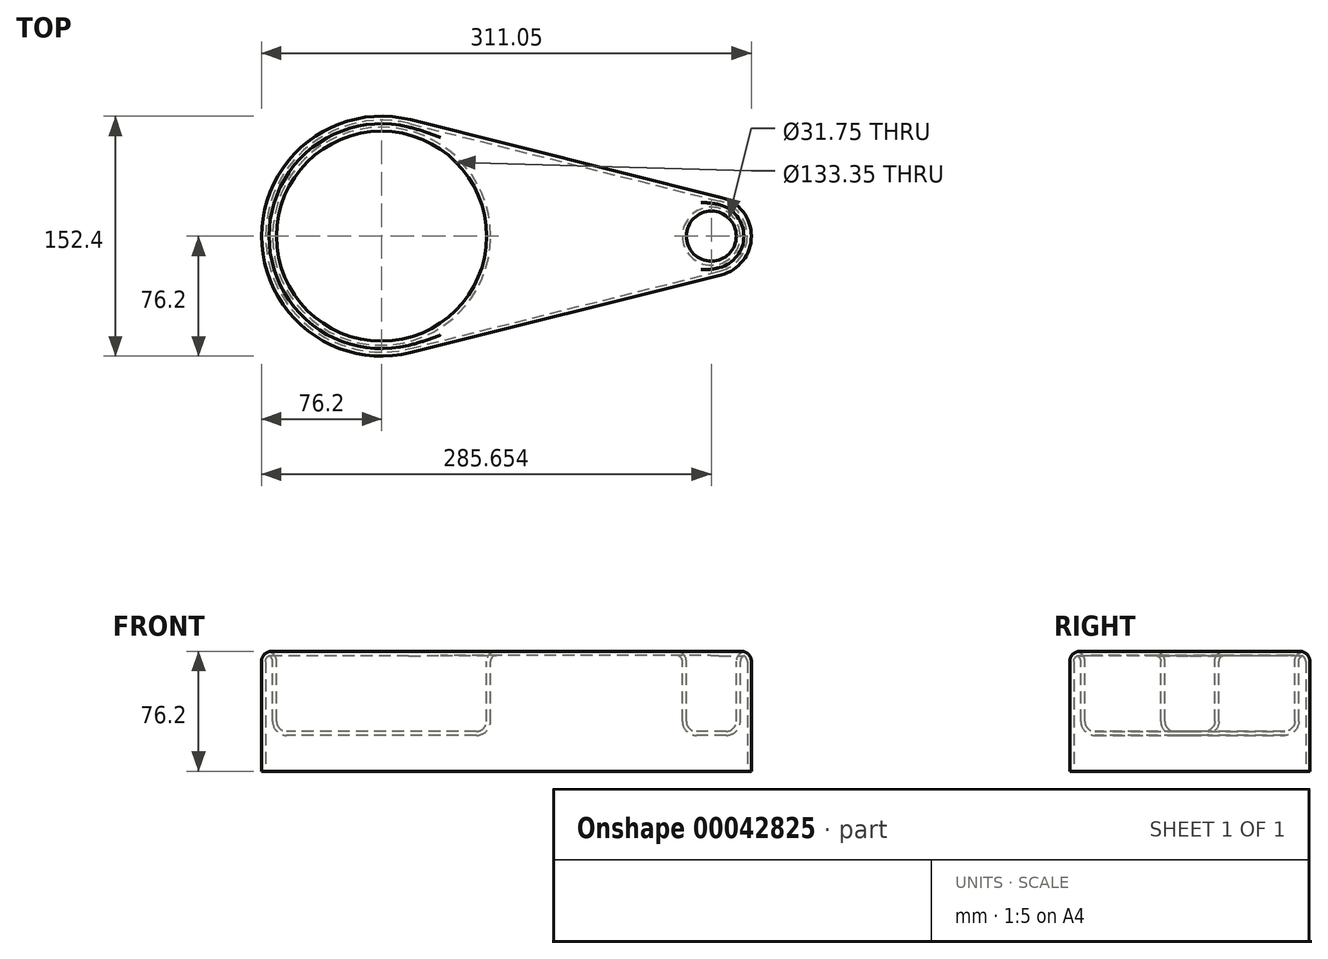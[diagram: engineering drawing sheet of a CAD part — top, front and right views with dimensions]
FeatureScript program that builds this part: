
annotation { "Feature Type Name" : "Feature", "Feature Type Description" : "" }
export const myFeature = defineFeature(function(context is Context, id is Id, definition is map)
    precondition{}
    {
        {
            var Q0;
            Q0=qCreatedBy(makeId("Top.planeOp"),FACE);
            var sketch = newSketch(context, id + "F0", { "sketchPlane" : qUnion([Q0])});
            skCircle(sketch, "E0", {"center": v(0, 0) * mm, "radius": 76.2 * mm});
            skCircle(sketch, "E1", {"center": v(209.45, 0) * mm, "radius": 25.4 * mm});
            skLineSegment(sketch, "E2", {"start": v(18.48, 73.92) * mm, "end": v(215.61, 24.64) * mm});
            skLineSegment(sketch, "E3", {"start": v(18.48, -73.92) * mm, "end": v(215.61, -24.64) * mm});
            skSolve(sketch);
        }
        {
            var Q0;
            {var subQ0=sQuery(id+"F0.wireOp",EDGE,"E0");var subQ2=makeQuery(id+"F0.imprint","INTERSECT",VERTEX,{"derivedFrom":[subQ0,sQuery(id+"F0.wireOp",EDGE,"E2")]});Q0=makeQuery(id+"F0.imprint","IMPRINT",FACE,{"disambiguationData":[TD([[makeQuery(id+"F0.imprint","IMPRINT",EDGE,{"disambiguationData":[TD([[subQ2,-1.0]])],"derivedFrom":subQ0}),1.0]])]});}
            var Q1;
            {var subQ1=sQuery(id+"F0.wireOp",EDGE,"E2");Q1=makeQuery(id+"F0.imprint","IMPRINT",FACE,{"disambiguationData":[TD([[makeQuery(id+"F0.imprint","IMPRINT",EDGE,{"derivedFrom":subQ1}),-1.0]])]});}
            var Q2;
            {var subQ0=sQuery(id+"F0.wireOp",EDGE,"E1");var subQ2=makeQuery(id+"F0.imprint","INTERSECT",VERTEX,{"derivedFrom":[subQ0,sQuery(id+"F0.wireOp",EDGE,"E2")]});Q2=makeQuery(id+"F0.imprint","IMPRINT",FACE,{"disambiguationData":[TD([[makeQuery(id+"F0.imprint","IMPRINT",EDGE,{"disambiguationData":[TD([[subQ2,-1.0]])],"derivedFrom":subQ0}),1.0]])]});}
            extrude(context, id + "F1", {"entities" : qUnion([Q0, Q1, Q2]), "depth" : 76.2 * mm});
        }
        {
            var Q0;
            Q0=makeQuery(id+"F1.opExtrude","CAP_FACE",FACE,{"disambiguationData":[OSD([sQuery(id+"F0.wireOp",EDGE,"E0"),sQuery(id+"F0.wireOp",EDGE,"E1"),sQuery(id+"F0.wireOp",EDGE,"E2"),sQuery(id+"F0.wireOp",EDGE,"E3")])],"isStart":false});
            var sketch = newSketch(context, id + "F2", { "sketchPlane" : qUnion([Q0])});
            skCircle(sketch, "E4", {"center": v(0, 0) * mm, "radius": 66.68 * mm});
            skCircle(sketch, "E5", {"center": v(209.45, 0) * mm, "radius": 15.88 * mm});
            skSolve(sketch);
        }
        {
            var Q0;
            Q0=makeQuery(id+"F2.imprint","IMPRINT",FACE,{"disambiguationData":[TD([[makeQuery(id+"F2.imprint","IMPRINT",EDGE,{"derivedFrom":sQuery(id+"F2.wireOp",EDGE,"E4")}),1.0]])]});
            var Q1;
            Q1=makeQuery(id+"F2.imprint","IMPRINT",FACE,{"disambiguationData":[TD([[makeQuery(id+"F2.imprint","IMPRINT",EDGE,{"derivedFrom":sQuery(id+"F2.wireOp",EDGE,"E5")}),1.0]])]});
            extrude(context, id + "F3", {"entities" : qUnion([Q0, Q1]), "operationType" : NewBodyOperationType.REMOVE, "oppositeDirection" : true, "depth" : 50.8 * mm});
        }
        {
            var Q0;
            Q0=makeQuery(id+"F1.opExtrude","CAP_FACE",FACE,{"disambiguationData":[OSD([sQuery(id+"F0.wireOp",EDGE,"E0"),sQuery(id+"F0.wireOp",EDGE,"E1"),sQuery(id+"F0.wireOp",EDGE,"E2"),sQuery(id+"F0.wireOp",EDGE,"E3")])],"isStart":false});
            var Q1;
            Q1=makeQuery(id+"F3.boolean.opBoolean","COPY",EDGE,{"derivedFrom":makeQuery(id+"F3.opExtrude","CAP_EDGE",EDGE,{"disambiguationData":[OSD([sQuery(id+"F2.wireOp",EDGE,"E4")])],"isStart":false})});
            var Q2;
            Q2=makeQuery(id+"F3.boolean.opBoolean","COPY",EDGE,{"derivedFrom":makeQuery(id+"F3.opExtrude","CAP_EDGE",EDGE,{"disambiguationData":[OSD([sQuery(id+"F2.wireOp",EDGE,"E5")])],"isStart":false})});
            fillet(context, id + "F4", {"entities" : qUnion([Q0, Q1, Q2]), "radius" : 6.35 * mm, "tangentPropagation" : true, "allowEdgeOverflow" : false});
        }
        {
            var Q0;
            Q0=makeQuery(id+"F1.opExtrude","CAP_FACE",FACE,{"disambiguationData":[OSD([sQuery(id+"F0.wireOp",EDGE,"E0"),sQuery(id+"F0.wireOp",EDGE,"E1"),sQuery(id+"F0.wireOp",EDGE,"E2"),sQuery(id+"F0.wireOp",EDGE,"E3")])],"isStart":true});
            shell(context, id + "F5", {"entities" : qUnion([Q0]), "thickness" : 2.54 * mm});
        }
    });
